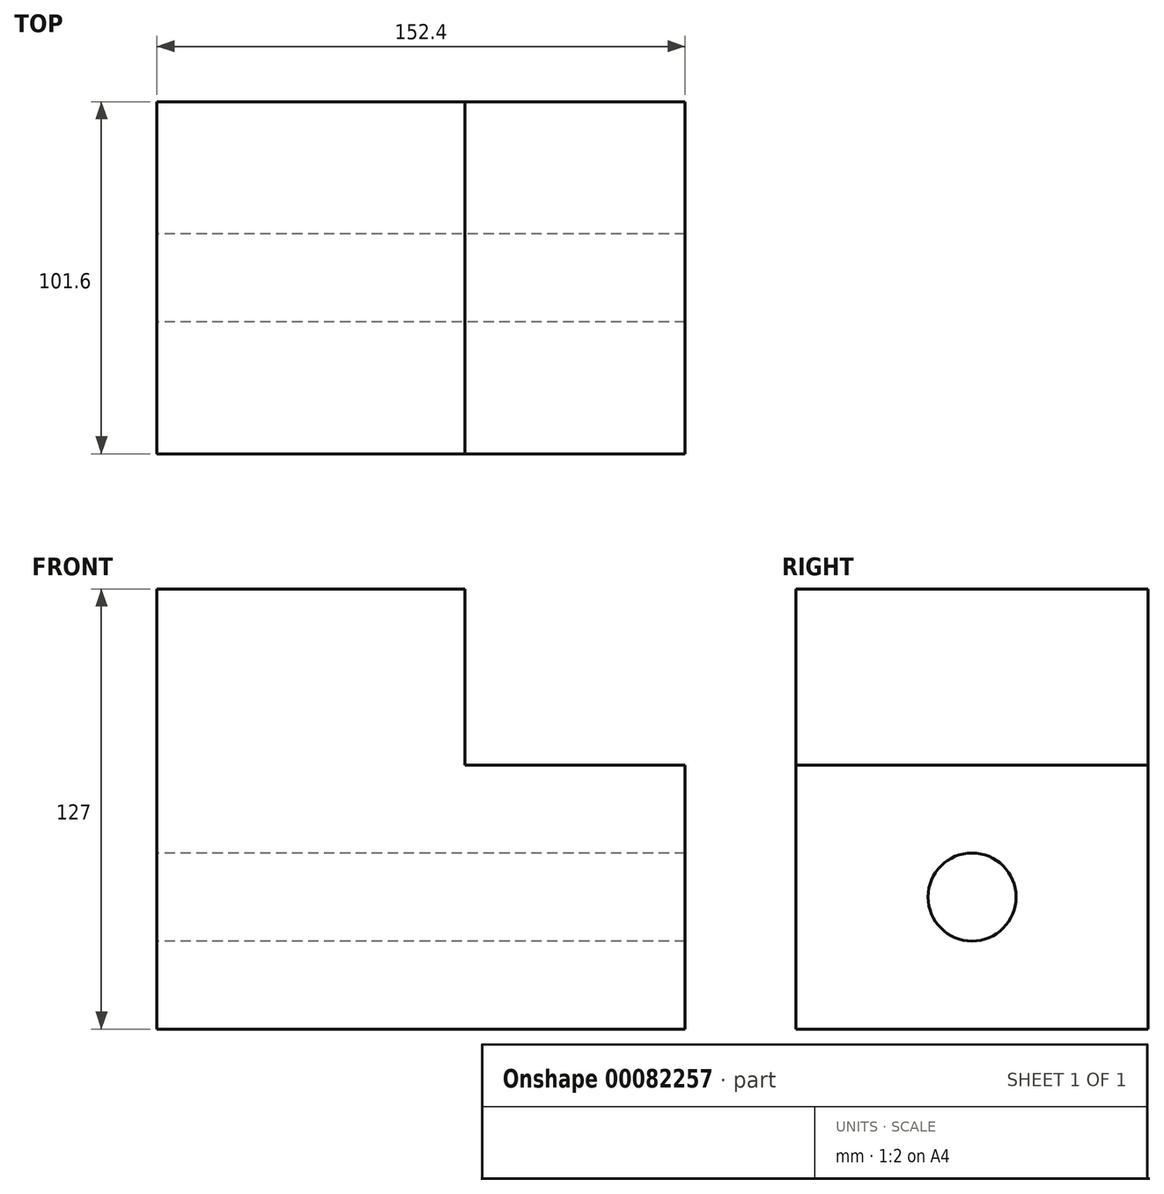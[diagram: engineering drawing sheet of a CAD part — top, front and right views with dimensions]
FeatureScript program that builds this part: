
annotation { "Feature Type Name" : "Feature", "Feature Type Description" : "" }
export const myFeature = defineFeature(function(context is Context, id is Id, definition is map)
    precondition{}
    {
        {
            var Q0;
            Q0=qCreatedBy(makeId("Top.planeOp"),FACE);
            var sketch = newSketch(context, id + "F0", { "sketchPlane" : qUnion([Q0])});
            skLineSegment(sketch, "E0.bottom", {"start": v(0, 0) * mm, "end": v(-152.4, 0) * mm});
            skLineSegment(sketch, "E0.top", {"start": v(0, -101.6) * mm, "end": v(-152.4, -101.6) * mm});
            skLineSegment(sketch, "E0.left", {"start": v(0, 0) * mm, "end": v(0, -101.6) * mm});
            skLineSegment(sketch, "E0.right", {"start": v(-152.4, 0) * mm, "end": v(-152.4, -101.6) * mm});
            skSolve(sketch);
        }
        {
            var Q0;
            Q0=makeQuery(id+"F0.imprint","IMPRINT",FACE,{"disambiguationData":[TD([[makeQuery(id+"F0.imprint","IMPRINT",EDGE,{"derivedFrom":sQuery(id+"F0.wireOp",EDGE,"E0.bottom")}),1.0]])]});
            extrude(context, id + "F1", {"entities" : qUnion([Q0]), "depth" : 127 * mm});
        }
        {
            var Q0;
            Q0=makeQuery(id+"F1.opExtrude","SWEPT_FACE",FACE,{"disambiguationData":[OSD([sQuery(id+"F0.wireOp",EDGE,"E0.top")])]});
            var sketch = newSketch(context, id + "F2", { "sketchPlane" : qUnion([Q0])});
            skLineSegment(sketch, "E1.bottom", {"start": v(0, 127) * mm, "end": v(-63.5, 127) * mm});
            skLineSegment(sketch, "E1.top", {"start": v(0, 76.2) * mm, "end": v(-63.5, 76.2) * mm});
            skLineSegment(sketch, "E1.left", {"start": v(0, 127) * mm, "end": v(0, 76.2) * mm});
            skLineSegment(sketch, "E1.right", {"start": v(-63.5, 127) * mm, "end": v(-63.5, 76.2) * mm});
            skSolve(sketch);
        }
        {
            var Q0;
            Q0 = qSketchRegion(id + "F2", true);
            extrude(context, id + "F3", {"entities" : qUnion([Q0]), "operationType" : NewBodyOperationType.REMOVE, "oppositeDirection" : true, "depth" : 101.6 * mm});
        }
        {
            var Q0;
            Q0=makeQuery(id+"F1.opExtrude","SWEPT_FACE",FACE,{"disambiguationData":[OSD([sQuery(id+"F0.wireOp",EDGE,"E0.right")])]});
            var sketch = newSketch(context, id + "F4", { "sketchPlane" : qUnion([Q0])});
            skCircle(sketch, "E2", {"center": v(50.8, 38.1) * mm, "radius": 12.7 * mm});
            skSolve(sketch);
        }
        {
            var Q0;
            Q0 = qSketchRegion(id + "F4", true);
            extrude(context, id + "F5", {"entities" : qUnion([Q0]), "operationType" : NewBodyOperationType.REMOVE, "oppositeDirection" : true, "depth" : 152.4 * mm});
        }
    });
